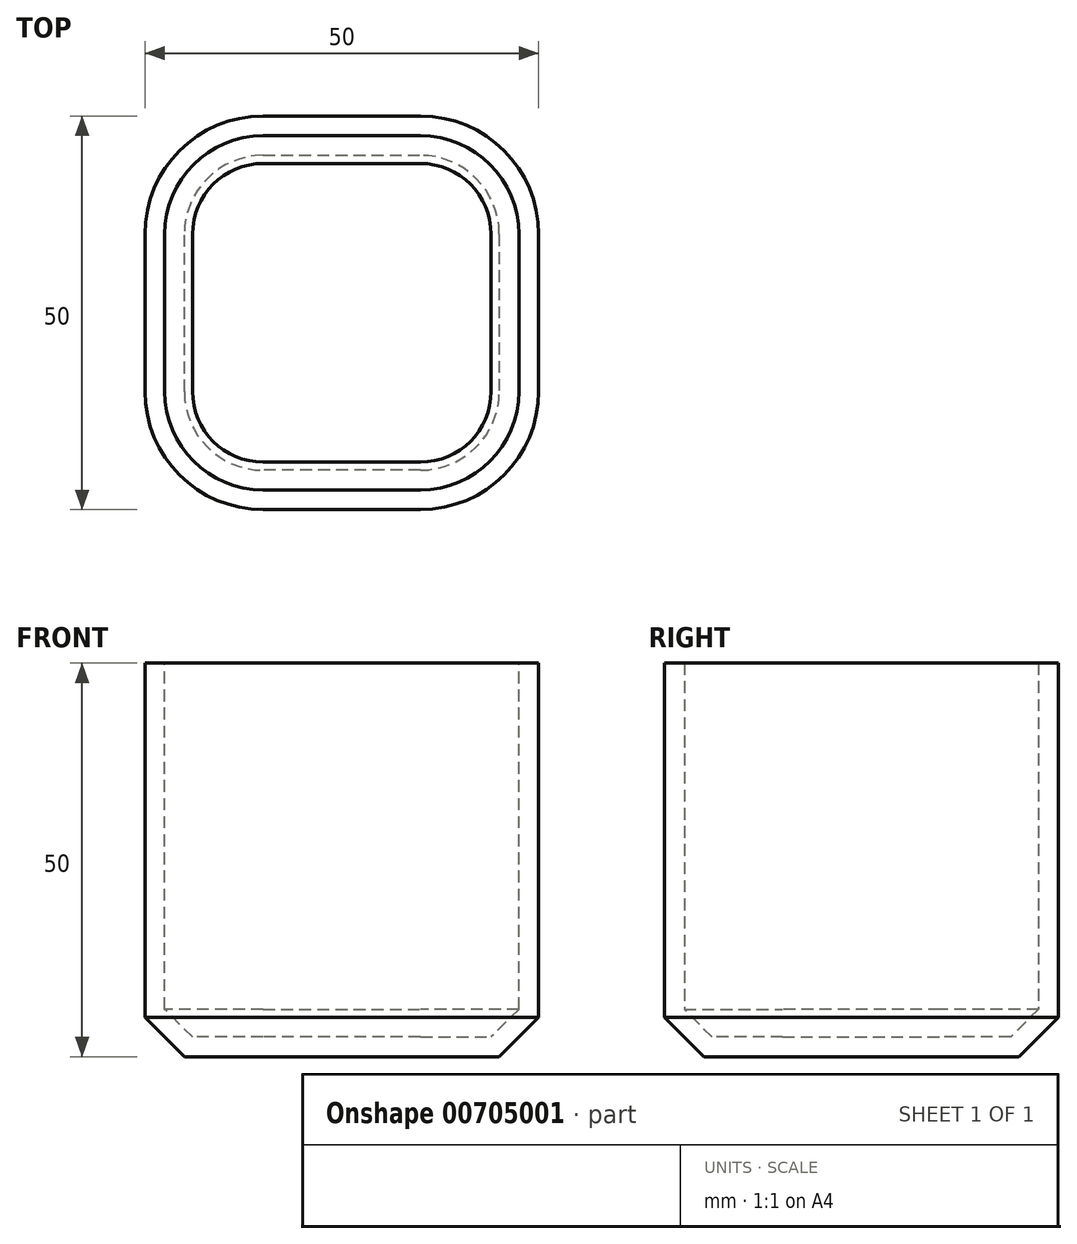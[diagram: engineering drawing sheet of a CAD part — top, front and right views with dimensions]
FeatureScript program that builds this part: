
annotation { "Feature Type Name" : "Feature", "Feature Type Description" : "" }
export const myFeature = defineFeature(function(context is Context, id is Id, definition is map)
    precondition{}
    {
        {
            var Q0;
            Q0=qCreatedBy(makeId("Top.planeOp"),FACE);
            var sketch = newSketch(context, id + "F0", { "sketchPlane" : qUnion([Q0])});
            skLineSegment(sketch, "E0.bottom", {"start": v(25, -25) * mm, "end": v(-25, -25) * mm});
            skLineSegment(sketch, "E0.top", {"start": v(25, 25) * mm, "end": v(-25, 25) * mm});
            skLineSegment(sketch, "E0.left", {"start": v(25, -25) * mm, "end": v(25, 25) * mm});
            skLineSegment(sketch, "E0.right", {"start": v(-25, -25) * mm, "end": v(-25, 25) * mm});
            skPoint(sketch, "E0.middle", {"position": v(0, 0) * mm});
            skSolve(sketch);
        }
        {
            var Q0;
            Q0 = qSketchRegion(id + "F0", true);
            extrude(context, id + "F1", {"entities" : qUnion([Q0]), "depth" : 50 * mm, "offsetDistance" : 25 * mm});
        }
        {
            var Q0;
            Q0=makeQuery(id+"F1.opExtrude","SWEPT_EDGE",EDGE,{"disambiguationData":[OSD([sQuery(id+"F0.wireOp",EDGE,"E0.bottom"),sQuery(id+"F0.wireOp",EDGE,"E0.right")])]});
            var Q1;
            Q1=makeQuery(id+"F1.opExtrude","SWEPT_EDGE",EDGE,{"disambiguationData":[OSD([sQuery(id+"F0.wireOp",EDGE,"E0.bottom"),sQuery(id+"F0.wireOp",EDGE,"E0.left")])]});
            var Q2;
            Q2=makeQuery(id+"F1.opExtrude","SWEPT_EDGE",EDGE,{"disambiguationData":[OSD([sQuery(id+"F0.wireOp",EDGE,"E0.top"),sQuery(id+"F0.wireOp",EDGE,"E0.left")])]});
            var Q3;
            Q3=makeQuery(id+"F1.opExtrude","SWEPT_EDGE",EDGE,{"disambiguationData":[OSD([sQuery(id+"F0.wireOp",EDGE,"E0.top"),sQuery(id+"F0.wireOp",EDGE,"E0.right")])]});
            fillet(context, id + "F2", {"entities" : qUnion([Q0, Q1, Q2, Q3]), "radius" : 15 * mm, "tangentPropagation" : true, "allowEdgeOverflow" : false});
        }
        {
            var Q0;
            {var subQ0=sQuery(id+"F0.wireOp",EDGE,"E0.left");var subQ1=sQuery(id+"F0.wireOp",EDGE,"E0.top");Q0=makeQuery(id+"F2.opFillet","BLEND_EDGE",EDGE,{"blendedFrom":[makeQuery(id+"F1.opExtrude","SWEPT_EDGE",EDGE,{"disambiguationData":[OSD([subQ1,subQ0])]}),makeQuery(id+"F1.opExtrude","CAP_FACE",FACE,{"disambiguationData":[OSD([sQuery(id+"F0.wireOp",EDGE,"E0.bottom"),subQ1,subQ0,sQuery(id+"F0.wireOp",EDGE,"E0.right")])],"isStart":true})],"blendedInto":[makeQuery(id+"F1.opExtrude","CAP_FACE",FACE,{"disambiguationData":[OSD([sQuery(id+"F0.wireOp",EDGE,"E0.bottom"),subQ1,subQ0,sQuery(id+"F0.wireOp",EDGE,"E0.right")])],"isStart":true})]});}
            var Q1;
            {var subQ0=sQuery(id+"F0.wireOp",EDGE,"E0.left");var subQ1=sQuery(id+"F0.wireOp",EDGE,"E0.bottom");Q1=makeQuery(id+"F2.opFillet","BLEND_EDGE",EDGE,{"blendedFrom":[makeQuery(id+"F1.opExtrude","SWEPT_EDGE",EDGE,{"disambiguationData":[OSD([subQ1,subQ0])]}),makeQuery(id+"F1.opExtrude","CAP_FACE",FACE,{"disambiguationData":[OSD([subQ1,sQuery(id+"F0.wireOp",EDGE,"E0.top"),subQ0,sQuery(id+"F0.wireOp",EDGE,"E0.right")])],"isStart":true})],"blendedInto":[makeQuery(id+"F1.opExtrude","CAP_FACE",FACE,{"disambiguationData":[OSD([subQ1,sQuery(id+"F0.wireOp",EDGE,"E0.top"),subQ0,sQuery(id+"F0.wireOp",EDGE,"E0.right")])],"isStart":true})]});}
            var Q2;
            {var subQ0=sQuery(id+"F0.wireOp",EDGE,"E0.right");var subQ1=sQuery(id+"F0.wireOp",EDGE,"E0.bottom");Q2=makeQuery(id+"F2.opFillet","BLEND_EDGE",EDGE,{"blendedFrom":[makeQuery(id+"F1.opExtrude","SWEPT_EDGE",EDGE,{"disambiguationData":[OSD([subQ1,subQ0])]}),makeQuery(id+"F1.opExtrude","CAP_FACE",FACE,{"disambiguationData":[OSD([subQ1,sQuery(id+"F0.wireOp",EDGE,"E0.top"),sQuery(id+"F0.wireOp",EDGE,"E0.left"),subQ0])],"isStart":true})],"blendedInto":[makeQuery(id+"F1.opExtrude","CAP_FACE",FACE,{"disambiguationData":[OSD([subQ1,sQuery(id+"F0.wireOp",EDGE,"E0.top"),sQuery(id+"F0.wireOp",EDGE,"E0.left"),subQ0])],"isStart":true})]});}
            var Q3;
            {var subQ0=sQuery(id+"F0.wireOp",EDGE,"E0.right");var subQ1=sQuery(id+"F0.wireOp",EDGE,"E0.top");Q3=makeQuery(id+"F2.opFillet","BLEND_EDGE",EDGE,{"blendedFrom":[makeQuery(id+"F1.opExtrude","SWEPT_EDGE",EDGE,{"disambiguationData":[OSD([subQ1,subQ0])]}),makeQuery(id+"F1.opExtrude","CAP_FACE",FACE,{"disambiguationData":[OSD([sQuery(id+"F0.wireOp",EDGE,"E0.bottom"),subQ1,sQuery(id+"F0.wireOp",EDGE,"E0.left"),subQ0])],"isStart":true})],"blendedInto":[makeQuery(id+"F1.opExtrude","CAP_FACE",FACE,{"disambiguationData":[OSD([sQuery(id+"F0.wireOp",EDGE,"E0.bottom"),subQ1,sQuery(id+"F0.wireOp",EDGE,"E0.left"),subQ0])],"isStart":true})]});}
            chamfer(context, id + "F3", {"entities" : qUnion([Q0, Q1, Q2, Q3]), "width" : 5 * mm, "tangentPropagation" : true});
        }
        {
            var Q0;
            Q0=makeQuery(id+"F1.opExtrude","CAP_FACE",FACE,{"disambiguationData":[OSD([sQuery(id+"F0.wireOp",EDGE,"E0.bottom"),sQuery(id+"F0.wireOp",EDGE,"E0.top"),sQuery(id+"F0.wireOp",EDGE,"E0.left"),sQuery(id+"F0.wireOp",EDGE,"E0.right")])],"isStart":false});
            shell(context, id + "F4", {"entities" : qUnion([Q0]), "thickness" : 2.5 * mm});
        }
    });
